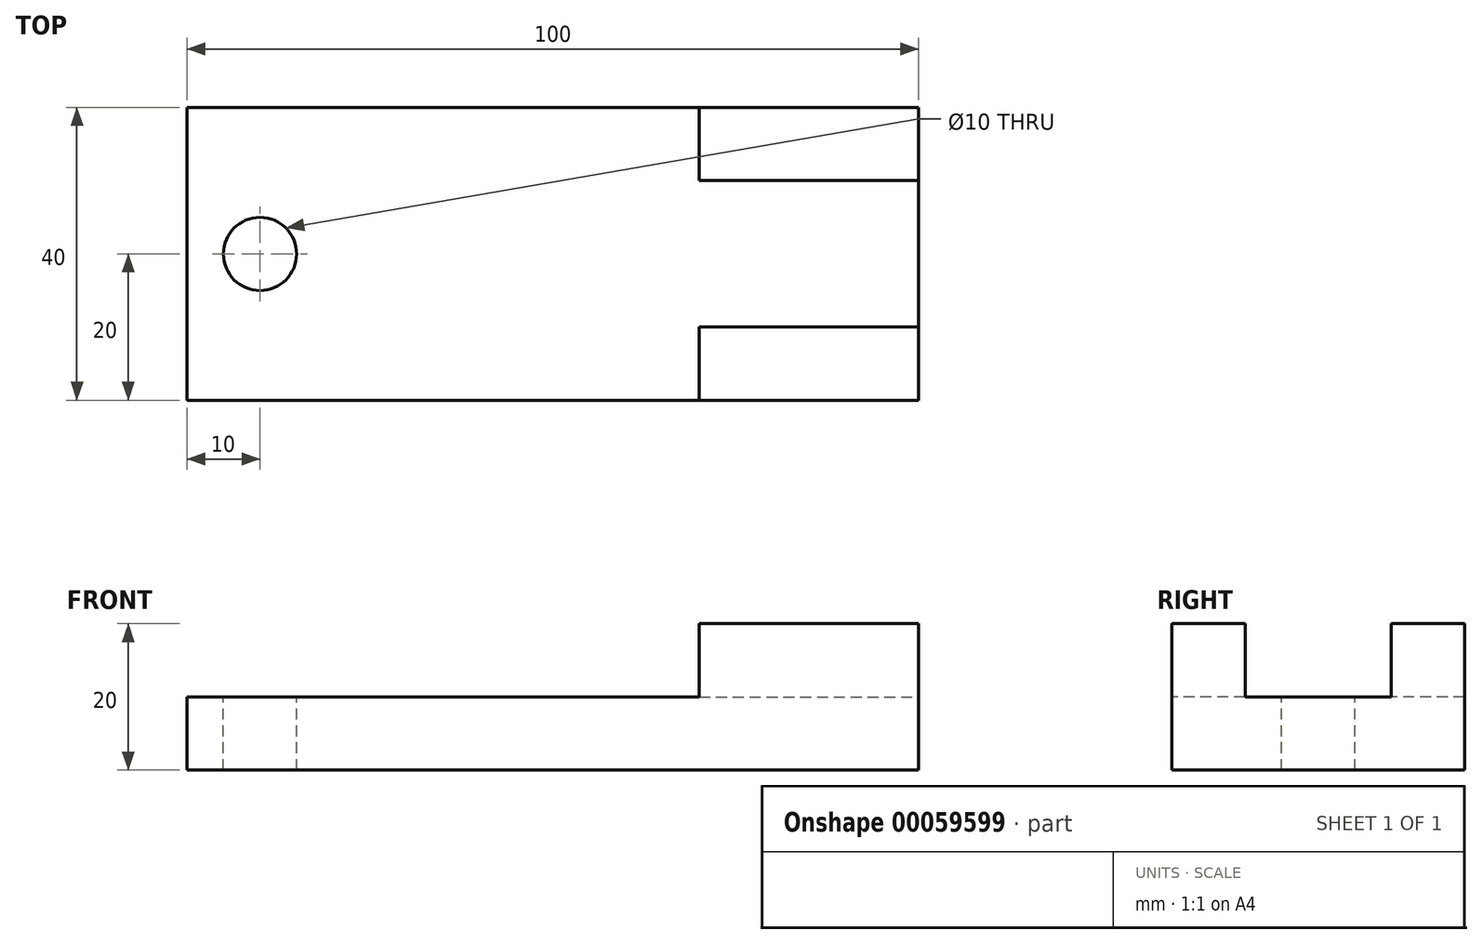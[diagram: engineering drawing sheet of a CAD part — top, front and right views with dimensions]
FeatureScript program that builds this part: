
annotation { "Feature Type Name" : "Feature", "Feature Type Description" : "" }
export const myFeature = defineFeature(function(context is Context, id is Id, definition is map)
    precondition{}
    {
        {
            var Q0;
            Q0=qCreatedBy(makeId("Top.planeOp"),FACE);
            var sketch = newSketch(context, id + "F0", { "sketchPlane" : qUnion([Q0])});
            skLineSegment(sketch, "E0.bottom", {"start": v(-10, 20) * mm, "end": v(90, 20) * mm});
            skLineSegment(sketch, "E0.top", {"start": v(-10, -20) * mm, "end": v(90, -20) * mm});
            skLineSegment(sketch, "E0.left", {"start": v(-10, 20) * mm, "end": v(-10, -20) * mm});
            skLineSegment(sketch, "E0.right", {"start": v(90, 20) * mm, "end": v(90, -20) * mm});
            skSolve(sketch);
        }
        {
            var Q0;
            Q0 = qSketchRegion(id + "F0", true);
            extrude(context, id + "F1", {"entities" : qUnion([Q0]), "depth" : 10 * mm});
        }
        {
            var Q0;
            Q0=makeQuery(id+"F1.opExtrude","CAP_FACE",FACE,{"disambiguationData":[OSD([sQuery(id+"F0.wireOp",EDGE,"E0.bottom"),sQuery(id+"F0.wireOp",EDGE,"E0.top"),sQuery(id+"F0.wireOp",EDGE,"E0.left"),sQuery(id+"F0.wireOp",EDGE,"E0.right")])],"isStart":false});
            var sketch = newSketch(context, id + "F2", { "sketchPlane" : qUnion([Q0])});
            skCircle(sketch, "E1", {"center": v(0, 0) * mm, "radius": 5 * mm});
            skSolve(sketch);
        }
        {
            var Q0;
            Q0 = qSketchRegion(id + "F2", true);
            extrude(context, id + "F3", {"entities" : qUnion([Q0]), "operationType" : NewBodyOperationType.REMOVE, "endBound" : BoundingType.UP_TO_NEXT, "oppositeDirection" : true, "depth" : 25 * mm});
        }
        {
            var Q0;
            Q0=makeQuery(id+"F1.opExtrude","CAP_FACE",FACE,{"disambiguationData":[OSD([sQuery(id+"F0.wireOp",EDGE,"E0.bottom"),sQuery(id+"F0.wireOp",EDGE,"E0.top"),sQuery(id+"F0.wireOp",EDGE,"E0.left"),sQuery(id+"F0.wireOp",EDGE,"E0.right")])],"isStart":false});
            var sketch = newSketch(context, id + "F4", { "sketchPlane" : qUnion([Q0])});
            skLineSegment(sketch, "E2.bottom", {"start": v(60, 20) * mm, "end": v(90, 20) * mm});
            skLineSegment(sketch, "E2.top", {"start": v(60, -20) * mm, "end": v(90, -20) * mm});
            skLineSegment(sketch, "E2.left", {"start": v(60, 20) * mm, "end": v(60, -20) * mm});
            skLineSegment(sketch, "E2.right", {"start": v(90, 20) * mm, "end": v(90, -20) * mm});
            skSolve(sketch);
        }
        {
            var Q0;
            Q0 = qSketchRegion(id + "F4", true);
            extrude(context, id + "F5", {"entities" : qUnion([Q0]), "operationType" : NewBodyOperationType.ADD, "depth" : 10 * mm});
        }
        {
            var Q0;
            Q0=makeQuery(id+"F5.opExtrude","CAP_FACE",FACE,{"disambiguationData":[OSD([sQuery(id+"F4.wireOp",EDGE,"E2.bottom"),sQuery(id+"F4.wireOp",EDGE,"E2.top"),sQuery(id+"F4.wireOp",EDGE,"E2.left"),sQuery(id+"F4.wireOp",EDGE,"E2.right")])],"isStart":false});
            var sketch = newSketch(context, id + "F6", { "sketchPlane" : qUnion([Q0])});
            skLineSegment(sketch, "E3.bottom", {"start": v(60, 10) * mm, "end": v(90, 10) * mm});
            skLineSegment(sketch, "E3.top", {"start": v(60, -10) * mm, "end": v(90, -10) * mm});
            skLineSegment(sketch, "E3.left", {"start": v(60, 10) * mm, "end": v(60, -10) * mm});
            skLineSegment(sketch, "E3.right", {"start": v(90, 10) * mm, "end": v(90, -10) * mm});
            skSolve(sketch);
        }
        {
            var Q0;
            Q0=makeQuery(id+"F6.imprint","IMPRINT",FACE,{"disambiguationData":[TD([[makeQuery(id+"F6.imprint","IMPRINT",EDGE,{"derivedFrom":sQuery(id+"F6.wireOp",EDGE,"E3.bottom")}),-1.0]])]});
            extrude(context, id + "F7", {"entities" : qUnion([Q0]), "operationType" : NewBodyOperationType.REMOVE, "oppositeDirection" : true, "depth" : 10 * mm});
        }
    });
